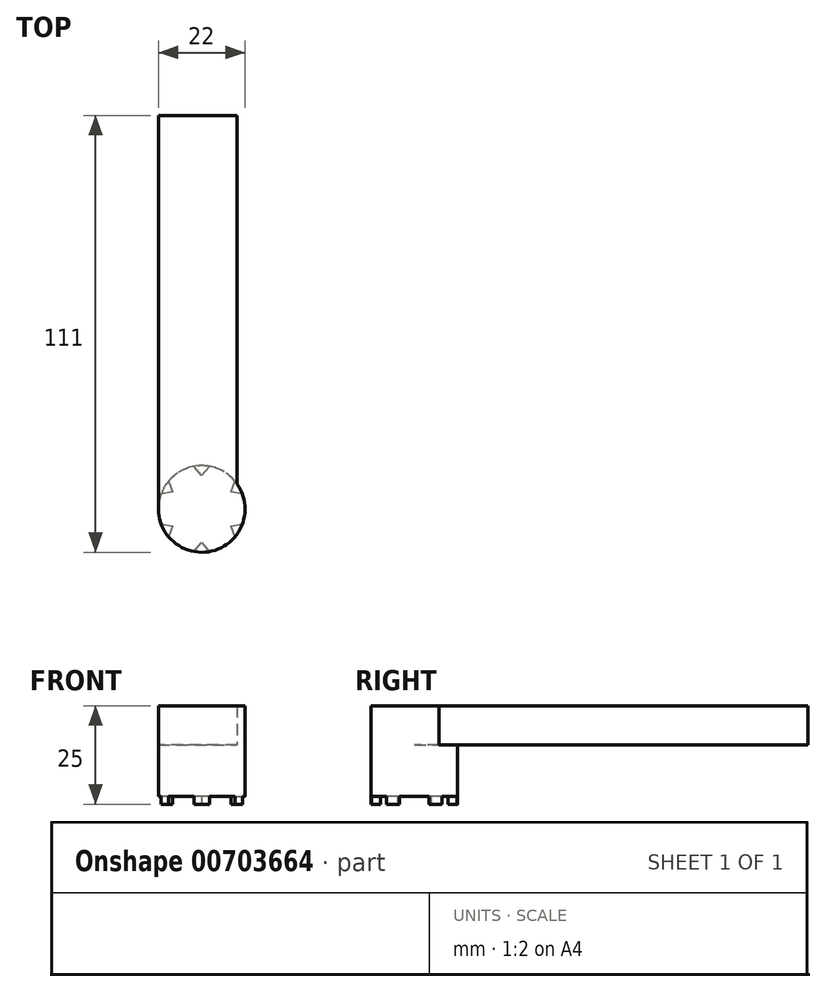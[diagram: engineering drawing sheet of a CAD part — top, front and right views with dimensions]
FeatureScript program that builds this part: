
annotation { "Feature Type Name" : "Feature", "Feature Type Description" : "" }
export const myFeature = defineFeature(function(context is Context, id is Id, definition is map)
    precondition{}
    {
        {
            var Q0;
            Q0=qCreatedBy(makeId("Top.planeOp"),FACE);
            var sketch = newSketch(context, id + "F0", { "sketchPlane" : qUnion([Q0])});
            skCircle(sketch, "E0", {"center": v(0, 0) * mm, "radius": 11 * mm});
            skLineSegment(sketch, "E1", {"start": v(0, 0) * mm, "end": v(11, 0) * mm, "construction": true});
            skLineSegment(sketch, "E2", {"start": v(11, 0) * mm, "end": v(0, 0) * mm, "construction": true});
            skLineSegment(sketch, "E3", {"start": v(0, 0) * mm, "end": v(-11, 0) * mm, "construction": true});
            skLineSegment(sketch, "E4.bottom", {"start": v(-11, 0) * mm, "end": v(9, 0) * mm});
            skLineSegment(sketch, "E4.top", {"start": v(-11, 100) * mm, "end": v(9, 100) * mm});
            skLineSegment(sketch, "E4.left", {"start": v(-11, 0) * mm, "end": v(-11, 100) * mm});
            skLineSegment(sketch, "E4.right", {"start": v(9, 0) * mm, "end": v(9, 100) * mm});
            skSolve(sketch);
        }
        {
            var Q0;
            {var subQ0=sQuery(id+"F0.wireOp",EDGE,"E4.bottom");Q0=makeQuery(id+"F0.imprint","IMPRINT",FACE,{"disambiguationData":[TD([[makeQuery(id+"F0.imprint","IMPRINT",EDGE,{"derivedFrom":subQ0}),-1.0]])]});}
            var Q1;
            {var subQ0=sQuery(id+"F0.wireOp",EDGE,"E4.bottom");Q1=makeQuery(id+"F0.imprint","IMPRINT",FACE,{"disambiguationData":[TD([[makeQuery(id+"F0.imprint","IMPRINT",EDGE,{"derivedFrom":subQ0}),1.0]])]});}
            extrude(context, id + "F1", {"entities" : qUnion([Q0, Q1]), "depth" : 20 * mm, "offsetDistance" : 25 * mm});
        }
        {
            var Q0;
            Q0 = qSketchRegion(id + "F0", true);
            extrude(context, id + "F2", {"entities" : qUnion([Q0]), "operationType" : NewBodyOperationType.ADD, "depth" : 25 * mm, "offsetDistance" : 25 * mm, "hasSecondDirection" : true, "secondDirectionOppositeDirection" : false, "secondDirectionDepth" : 15 * mm});
        }
        {
            var Q0;
            Q0=qCreatedBy(makeId("Top.planeOp"),FACE);
            var sketch = newSketch(context, id + "F3", { "sketchPlane" : qUnion([Q0])});
            skLineSegment(sketch, "E5.0", {"start": v(7.38, -4.26) * mm, "end": v(15.69, -2.83) * mm});
            skLineSegment(sketch, "E5.1", {"start": v(10.3, -12.17) * mm, "end": v(7.38, -4.26) * mm});
            skArc(sketch, "E5.2", {"start": v(5.4, -15) * mm, "mid": v(9.04, -15.65) * mm, "end": v(10.3, -12.17) * mm});
            skLineSegment(sketch, "E5.3", {"start": v(0, -8.53) * mm, "end": v(5.4, -15) * mm});
            skLineSegment(sketch, "E5.4", {"start": v(-5.4, -15) * mm, "end": v(0, -8.53) * mm});
            skArc(sketch, "E5.5", {"start": v(15.69, -2.83) * mm, "mid": v(18.07, 0) * mm, "end": v(15.69, 2.83) * mm});
            skArc(sketch, "E5.6", {"start": v(-10.3, -12.17) * mm, "mid": v(-9.04, -15.65) * mm, "end": v(-5.4, -15) * mm});
            skLineSegment(sketch, "E5.7", {"start": v(-7.38, -4.26) * mm, "end": v(-10.3, -12.17) * mm});
            skLineSegment(sketch, "E5.8", {"start": v(5.4, 15) * mm, "end": v(0, 8.53) * mm});
            skArc(sketch, "E5.9", {"start": v(10.3, 12.17) * mm, "mid": v(9.04, 15.65) * mm, "end": v(5.4, 15) * mm});
            skLineSegment(sketch, "E5.10", {"start": v(7.38, 4.26) * mm, "end": v(10.3, 12.17) * mm});
            skLineSegment(sketch, "E5.11", {"start": v(15.69, 2.83) * mm, "end": v(7.38, 4.26) * mm});
            skLineSegment(sketch, "E5.12", {"start": v(0, 8.53) * mm, "end": v(-5.4, 15) * mm});
            skArc(sketch, "E5.13", {"start": v(-5.4, 15) * mm, "mid": v(-9.04, 15.65) * mm, "end": v(-10.3, 12.17) * mm});
            skLineSegment(sketch, "E5.14", {"start": v(-10.3, 12.17) * mm, "end": v(-7.38, 4.26) * mm});
            skLineSegment(sketch, "E5.15", {"start": v(-7.38, 4.26) * mm, "end": v(-15.69, 2.83) * mm});
            skArc(sketch, "E5.16", {"start": v(-15.69, 2.83) * mm, "mid": v(-18.07, 0) * mm, "end": v(-15.69, -2.83) * mm});
            skLineSegment(sketch, "E5.17", {"start": v(-15.69, -2.83) * mm, "end": v(-7.38, -4.26) * mm});
            skCircle(sketch, "E6", {"center": v(0, 0) * mm, "radius": 12.5 * mm});
            skSolve(sketch);
        }
        {
            var Q0;
            {var subQ13=sQuery(id+"F3.wireOp",EDGE,"E5.1");var subQ14=sQuery(id+"F3.wireOp",EDGE,"E5.0");var subQ15=makeQuery(id+"F3.imprint","INTERSECT",VERTEX,{"derivedFrom":[subQ14,subQ13]});Q0=makeQuery(id+"F3.imprint","IMPRINT",FACE,{"disambiguationData":[TD([[makeQuery(id+"F3.imprint","IMPRINT",EDGE,{"disambiguationData":[TD([[subQ15,-1.0]])],"derivedFrom":subQ14}),1.0]])]});}
            extrude(context, id + "F4", {"entities" : qUnion([Q0]), "operationType" : NewBodyOperationType.REMOVE, "depth" : 2 * mm, "offsetDistance" : 25 * mm});
        }
    });
